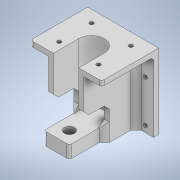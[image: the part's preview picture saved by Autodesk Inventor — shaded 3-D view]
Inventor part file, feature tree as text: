
AUTODESK INVENTOR PART (.ipt)
format: ipt  version: 2022 (Build 260153000, 153)  size: 357,376 bytes
history: native  units: mm
features: sketch x18, extrude x17, chamfer x4, hole x3, fillet x2, other x1
ambient origin geometry x8: Origin, YZ Plane, XZ Plane, XY Plane, X Axis, Y Axis, Z Axis, Center Point
bodies: Body1 (feature_tree)
feature tree (45):
  other  "Sólido1"
  sketch  "Esboço1"  dims[d0=56.0mm d1=10.0mm]
  extrude  "Extrusão1"  Depth=10.0mm
  extrude  "Extrusão2"  Depth=4.0mm TaperAngle=0.0deg
  hole  "Furo1"  [1 undecoded]
  hole  "Furo2"  [1 undecoded]
  extrude  "Extrusão3"  Depth=15.5mm
  extrude  "Extrusão4"  Depth=15.5mm
  sketch  "Esboço6"  dims[d25=25.0mm d26=39.0mm d27=0.0mm]
  extrude  "Extrusão5"  Depth=20.0mm
  extrude  "Extrusão6"  Depth=3.0mm
  extrude  "Extrusão7"  Depth=3.0mm
  extrude  "Extrusão8"  Depth=20.0mm TaperAngle=0.0deg
  extrude  "Extrusão9"  Depth=14.0mm TaperAngle=0.0deg
  extrude  "Extrusão10"  Depth=14.0mm TaperAngle=0.0deg
  chamfer  "Chanfro2"  Distance=39.0mm
  fillet  "Arredondamento1"  Radius=10.0mm
  hole  "Furo3"  [1 undecoded]
  extrude  "Extrusão11"  Depth=10.0mm TaperAngle=0.0deg
  fillet  "Arredondamento2"  Radius=2.0mm
  extrude  "Extrusão12"  Depth=4.0mm
  extrude  "Extrusão13"  Depth=14.0mm TaperAngle=0.0deg
  extrude  "Extrusão14"  Depth=4.0mm
  chamfer  "Chanfro3"  Distance=14.0mm
  extrude  "Extrusão15"  Depth=4.0mm TaperAngle=45.0deg
  chamfer  "Chanfro4"  [1 undecoded]
  extrude  "Extrusão16"  Depth=4.0mm TaperAngle=45.0deg
  extrude  "Extrusão17"  Depth=2.0mm
  chamfer  "Chanfro5"  Distance=4.0mm
  sketch  "Esboço2"  dims[d2=20.0mm d3=4.0mm d4=0.0mm]
  sketch  "Esboço3"  dims[d5=52.426mm d6=0.0mm]
  sketch  "Esboço4"  dims[d10=8.0mm d11=6.0mm d12=4.0mm d13=2.0mm d14=90.0deg d15=8.0mm d16=20.594885mm]
  sketch  "Esboço5"  dims[d17=3.0mm d18=6.0mm d19=4.0mm d20=2.0mm d21=90.0deg d22=8.0mm d23=20.594885mm d24=10.0mm]
  sketch  "Esboço7"  dims[d28=22.0mm d29=0.0mm d30=15.5mm]
  sketch  "Esboço8"  dims[d31=15.5mm d32=15.5mm]
  sketch  "Esboço9"  dims[d33=15.5mm d34=20.0mm]
  sketch  "Esboço10"  dims[d35=0.0mm d36=0.0mm d37=3.0mm]
  sketch  "Esboço11"  dims[d38=3.0mm d39=3.0mm]
  sketch  "Esboço12"  dims[d40=3.0mm d41=20.0mm d42=0.0mm]
  sketch  "Esboço13"  dims[d43=4.0mm d44=14.0mm d45=0.0mm]
  sketch  "Esboço14"  dims[d46=4.0mm d47=14.0mm d48=0.0mm d49=39.0mm d50=0.0mm d51=10.0mm d52=0.0mm]
  sketch  "Esboço15"  dims[d53=4.0mm d54=2.0mm d55=45.0deg d56=2.0mm]
  sketch  "Esboço16"  dims[d57=33.0mm]
  sketch  "Esboço17"  dims[d58=3.0mm d59=6.0mm d60=4.0mm d61=2.0mm d62=90.0deg d63=8.0mm d64=20.594885mm d65=10.0mm d66=0.0mm d67=2.0mm]
  sketch  "Esboço18"  dims[d68=0.0mm d69=0.0mm d70=4.0mm d71=14.0mm d72=0.0mm d73=4.0mm d74=14.0mm d75=0.0mm d76=4.0mm d77=2.0mm d78=45.0deg d79=0.0mm d80=0.0mm d81=4.0mm d82=2.0mm d83=45.0deg d84=2.5mm d85=4.0mm d86=5.0mm d87=2.5mm d88=4.0mm d89=5.0mm d90=2.0mm d91=0.0mm d92=2.5mm d93=4.0mm d94=5.0mm d95=2.5mm d96=4.0mm d97=5.0mm d98=2.0mm d99=0.0mm d100=2.0mm d101=2.0mm d102=45.0deg]
note: 4 required parameter values undecoded (feature->parameter linkage not recoverable at this tier; creation-order binding heuristic only, values carry confidence <= 0.55)
